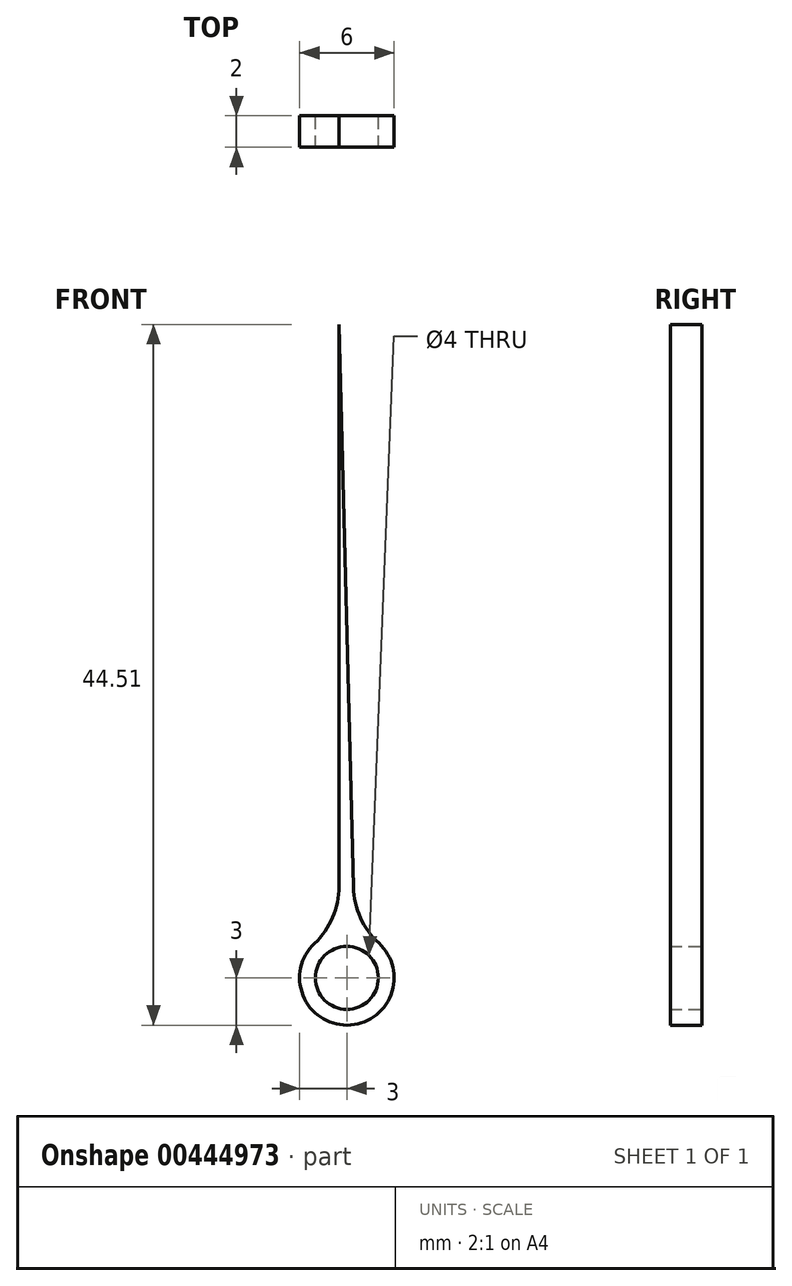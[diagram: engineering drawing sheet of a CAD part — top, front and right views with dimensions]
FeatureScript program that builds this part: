
annotation { "Feature Type Name" : "Feature", "Feature Type Description" : "" }
export const myFeature = defineFeature(function(context is Context, id is Id, definition is map)
    precondition{}
    {
        {
            var Q0;
            Q0=qCreatedBy(makeId("Front.planeOp"),FACE);
            var sketch = newSketch(context, id + "F0", { "sketchPlane" : qUnion([Q0])});
            skCircle(sketch, "E0", {"center": v(0, 0) * mm, "radius": 2 * mm});
            skArc(sketch, "E1", {"start": v(-2.06, 2.18) * mm, "mid": v(0.02, -3) * mm, "end": v(2.03, 2.2) * mm});
            skLineSegment(sketch, "E2", {"start": v(-0.49, 5.82) * mm, "end": v(-0.49, 41.5) * mm});
            skLineSegment(sketch, "E3", {"start": v(-0.49, 41.5) * mm, "end": v(0.42, 5.76) * mm});
            skPoint(sketch, "E4.visualSharp", {"position": v(-0.49, 2.96) * mm});
            skArc(sketch, "E4.filletArc", {"start": v(-2.06, 2.18) * mm, "mid": v(-0.9, 3.84) * mm, "end": v(-0.49, 5.82) * mm});
            skPoint(sketch, "E5.visualSharp", {"position": v(0.49, 2.96) * mm});
            skArc(sketch, "E5.filletArc", {"start": v(0.42, 5.76) * mm, "mid": v(0.86, 3.82) * mm, "end": v(2.03, 2.2) * mm});
            skSolve(sketch);
        }
        {
            var Q0;
            Q0 = qSketchRegion(id + "F0", true);
            extrude(context, id + "F1", {"entities" : qUnion([Q0]), "depth" : 2 * mm});
        }
    });
